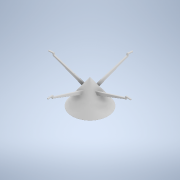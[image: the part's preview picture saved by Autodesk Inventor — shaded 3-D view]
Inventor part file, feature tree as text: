
AUTODESK INVENTOR PART (.ipt)
format: ipt  version: 2020.1 (Build 241239000, 239)  size: 567,808 bytes
history: native  units: mm
features: fillet x2, sketch x2, other x1, revolve x1, extrude x1, pattern_circular x1
ambient origin geometry x8: Origin, YZ Plane, XZ Plane, XY Plane, X Axis, Y Axis, Z Axis, Center Point
bodies: Body1 (feature_tree)
feature tree (8):
  other  "Sólido1"
  revolve  "Revolución1"  [1 undecoded]
  extrude  "Extrusión5"  Depth=0.5mm
  fillet  "Empalme3"  [1 undecoded]
  pattern_circular  "Patrón circular2"  [2 undecoded]
  fillet  "Empalme4"  Radius=29.0mm
  sketch  "Boceto3"  dims[d3=69.0mm d4=49.5mm]
  sketch  "Boceto9"  dims[d5=47.0mm d7=2.5mm d8=90.0deg d18=1.5mm d26=29.0mm d27=10.0mm d29=99.0mm d30=4.0mm d31=3.5mm d32=0.0mm d33=5.0mm d34=75.0deg d35=3.0mm d36=75.0deg d37=14.5mm d39=3.0mm d40=105.0deg d45=1.0mm d46=40.0mm d47=360.0deg d49=0.5mm]
note: 4 required parameter values undecoded (feature->parameter linkage not recoverable at this tier; creation-order binding heuristic only, values carry confidence <= 0.55)